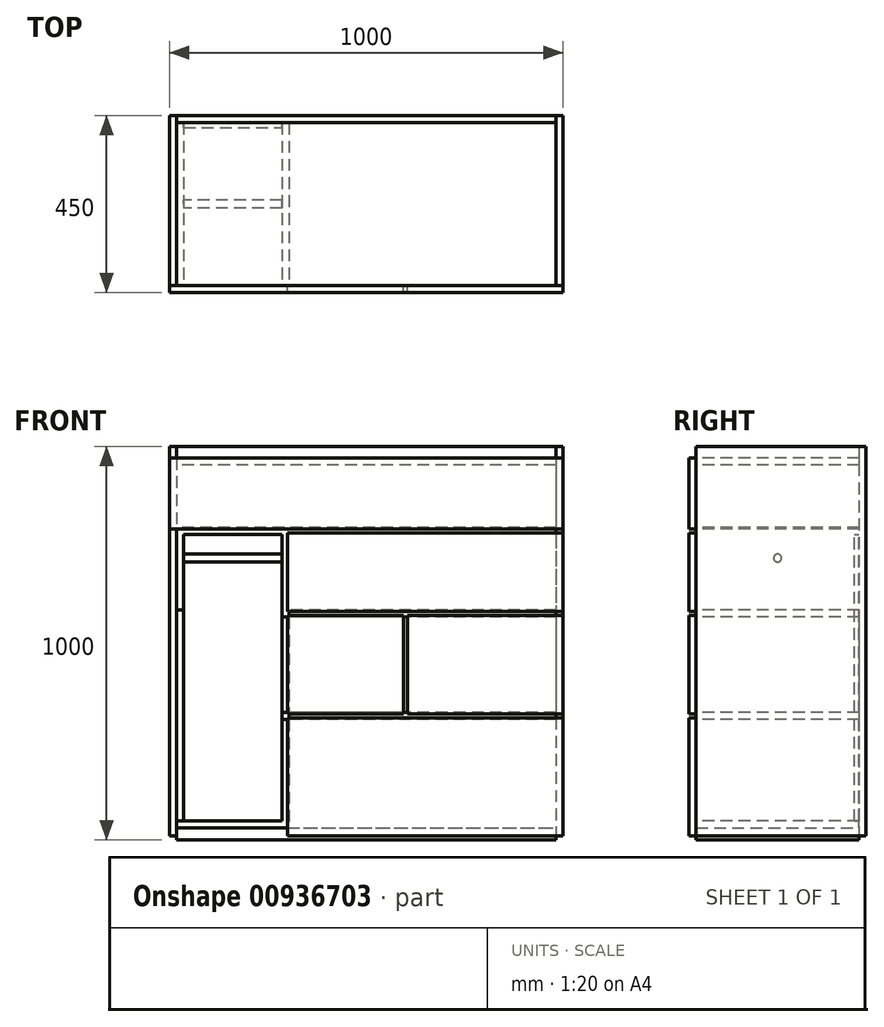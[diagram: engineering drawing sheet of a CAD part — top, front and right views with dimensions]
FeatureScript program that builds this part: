
annotation { "Feature Type Name" : "Feature", "Feature Type Description" : "" }
export const myFeature = defineFeature(function(context is Context, id is Id, definition is map)
    precondition{}
    {
        {
            var Q0;
            Q0=qCreatedBy(makeId("Top.planeOp"),FACE);
            var sketch = newSketch(context, id + "F0", { "sketchPlane" : qUnion([Q0])});
            skLineSegment(sketch, "E0.bottom", {"start": v(0, 0) * mm, "end": v(1000, 0) * mm});
            skLineSegment(sketch, "E0.top", {"start": v(0, 432) * mm, "end": v(1000, 432) * mm});
            skLineSegment(sketch, "E0.left", {"start": v(0, 0) * mm, "end": v(0, 432) * mm});
            skLineSegment(sketch, "E0.right", {"start": v(1000, 0) * mm, "end": v(1000, 432) * mm});
            skLineSegment(sketch, "E1.0", {"start": v(18, 0) * mm, "end": v(18, 432) * mm});
            skLineSegment(sketch, "E2", {"start": v(500, 467.89) * mm, "end": v(500, 549.02) * mm, "construction": true});
            skPoint(sketch, "E2.startSnap0", {"position": v(500, 432) * mm});
            skLineSegment(sketch, "E3.MirrorCS", {"start": v(982, 0) * mm, "end": v(982, 432) * mm});
            skLineSegment(sketch, "E4", {"start": v(1028.28, 216) * mm, "end": v(1100.38, 216) * mm, "construction": true});
            skPoint(sketch, "E4.startSnap0", {"position": v(1000, 216) * mm});
            skLineSegment(sketch, "E5.0", {"start": v(0, 414) * mm, "end": v(1000, 414) * mm});
            skSolve(sketch);
        }
        {
            var Q0;
            {var subQ0=sQuery(id+"F0.wireOp",EDGE,"E0.left");var subQ1=sQuery(id+"F0.wireOp",EDGE,"E0.bottom");var subQ2=makeQuery(id+"F0.imprint","INTERSECT",VERTEX,{"derivedFrom":[subQ1,subQ0]});Q0=makeQuery(id+"F0.imprint","IMPRINT",FACE,{"disambiguationData":[TD([[makeQuery(id+"F0.imprint","IMPRINT",EDGE,{"disambiguationData":[TD([[subQ2,-1.0]])],"derivedFrom":subQ1}),1.0]])]});}
            var Q1;
            {var subQ0=sQuery(id+"F0.wireOp",EDGE,"E0.left");var subQ1=sQuery(id+"F0.wireOp",EDGE,"E0.top");var subQ2=makeQuery(id+"F0.imprint","INTERSECT",VERTEX,{"derivedFrom":[subQ1,subQ0]});Q1=makeQuery(id+"F0.imprint","IMPRINT",FACE,{"disambiguationData":[TD([[makeQuery(id+"F0.imprint","IMPRINT",EDGE,{"disambiguationData":[TD([[subQ2,-1.0]])],"derivedFrom":subQ1}),-1.0]])]});}
            var Q2;
            {var subQ0=sQuery(id+"F0.wireOp",EDGE,"E0.right");var subQ1=sQuery(id+"F0.wireOp",EDGE,"E0.top");var subQ2=makeQuery(id+"F0.imprint","INTERSECT",VERTEX,{"derivedFrom":[subQ1,subQ0]});Q2=makeQuery(id+"F0.imprint","IMPRINT",FACE,{"disambiguationData":[TD([[makeQuery(id+"F0.imprint","IMPRINT",EDGE,{"disambiguationData":[TD([[subQ2,1.0]])],"derivedFrom":subQ1}),-1.0]])]});}
            var Q3;
            {var subQ0=sQuery(id+"F0.wireOp",EDGE,"E0.right");var subQ1=sQuery(id+"F0.wireOp",EDGE,"E0.bottom");var subQ2=makeQuery(id+"F0.imprint","INTERSECT",VERTEX,{"derivedFrom":[subQ1,subQ0]});Q3=makeQuery(id+"F0.imprint","IMPRINT",FACE,{"disambiguationData":[TD([[makeQuery(id+"F0.imprint","IMPRINT",EDGE,{"disambiguationData":[TD([[subQ2,1.0]])],"derivedFrom":subQ1}),1.0]])]});}
            extrude(context, id + "F1", {"entities" : qUnion([Q0, Q1, Q2, Q3]), "depth" : 990 * mm, "offsetDistance" : 25 * mm});
        }
        {
            var Q0;
            {var subQ0=sQuery(id+"F0.wireOp",EDGE,"E1.0");var subQ1=sQuery(id+"F0.wireOp",EDGE,"E0.top");var subQ2=makeQuery(id+"F0.imprint","INTERSECT",VERTEX,{"derivedFrom":[subQ1,subQ0]});Q0=makeQuery(id+"F0.imprint","IMPRINT",FACE,{"disambiguationData":[TD([[makeQuery(id+"F0.imprint","IMPRINT",EDGE,{"disambiguationData":[TD([[subQ2,-1.0]])],"derivedFrom":subQ1}),-1.0]])]});}
            var Q1;
            Q1=makeQuery(id+"F1.opExtrude","CAP_FACE",FACE,{"disambiguationData":[OSD([sQuery(id+"F0.wireOp",EDGE,"E0.bottom"),sQuery(id+"F0.wireOp",EDGE,"E0.top"),sQuery(id+"F0.wireOp",EDGE,"E0.left"),sQuery(id+"F0.wireOp",EDGE,"E1.0")])],"isStart":false});
            extrude(context, id + "F2", {"entities" : qUnion([Q0]), "endBound" : BoundingType.UP_TO_SURFACE, "depth" : 25 * mm, "endBoundEntityFace" : qUnion([Q1]), "offsetDistance" : 25 * mm});
        }
        {
            var Q0;
            {var subQ0=sQuery(id+"F0.wireOp",EDGE,"E1.0");var subQ1=sQuery(id+"F0.wireOp",EDGE,"E0.bottom");var subQ2=makeQuery(id+"F0.imprint","INTERSECT",VERTEX,{"derivedFrom":[subQ1,subQ0]});Q0=makeQuery(id+"F0.imprint","IMPRINT",FACE,{"disambiguationData":[TD([[makeQuery(id+"F0.imprint","IMPRINT",EDGE,{"disambiguationData":[TD([[subQ2,-1.0]])],"derivedFrom":subQ1}),1.0]])]});}
            extrude(context, id + "F3", {"entities" : qUnion([Q0]), "depth" : 20 * mm, "offsetDistance" : 25 * mm, "hasSecondDirection" : true, "secondDirectionOppositeDirection" : true, "secondDirectionDepth" : 10 * mm});
        }
        {
            var Q0;
            {var subQ0=sQuery(id+"F0.wireOp",EDGE,"E0.bottom");Q0=makeQuery(id+"F1.opExtrude","SWEPT_FACE",FACE,{"disambiguationData":[OSD([subQ0]),TDD([makeQuery(id+"F0.imprint","IMPRINT",EDGE,{"disambiguationData":[TD([[makeQuery(id+"F0.imprint","INTERSECT",VERTEX,{"derivedFrom":[subQ0,sQuery(id+"F0.wireOp",EDGE,"E0.left")]}),-1.0]])],"derivedFrom":subQ0})])]});}
            var sketch = newSketch(context, id + "F4", { "sketchPlane" : qUnion([Q0])});
            skLineSegment(sketch, "E6.bottom", {"start": v(1000, 560) * mm, "end": v(605, 560) * mm});
            skLineSegment(sketch, "E6.top", {"start": v(1000, 310) * mm, "end": v(605, 310) * mm});
            skLineSegment(sketch, "E6.left", {"start": v(1000, 560) * mm, "end": v(1000, 310) * mm});
            skLineSegment(sketch, "E6.right", {"start": v(605, 560) * mm, "end": v(605, 310) * mm});
            skLineSegment(sketch, "E7.bottom", {"start": v(595, 560) * mm, "end": v(0, 560) * mm});
            skLineSegment(sketch, "E7.top", {"start": v(595, 310) * mm, "end": v(0, 310) * mm});
            skLineSegment(sketch, "E7.left", {"start": v(595, 560) * mm, "end": v(595, 310) * mm});
            skLineSegment(sketch, "E7.right", {"start": v(0, 560) * mm, "end": v(0, 310) * mm});
            skLineSegment(sketch, "E8", {"start": v(605, 435) * mm, "end": v(595, 435) * mm, "construction": true});
            skLineSegment(sketch, "E9.bottom", {"start": v(0, 300) * mm, "end": v(290, 300) * mm});
            skLineSegment(sketch, "E9.top", {"start": v(0, 0) * mm, "end": v(290, 0) * mm});
            skLineSegment(sketch, "E9.right", {"start": v(290, 300) * mm, "end": v(290, 0) * mm});
            skLineSegment(sketch, "E10.bottom", {"start": v(300, 300) * mm, "end": v(1000, 300) * mm});
            skLineSegment(sketch, "E10.top", {"start": v(300, 0) * mm, "end": v(1000, 0) * mm});
            skLineSegment(sketch, "E10.left", {"start": v(300, 300) * mm, "end": v(300, 0) * mm});
            skLineSegment(sketch, "E10.right", {"start": v(1000, 300) * mm, "end": v(1000, 0) * mm});
            skLineSegment(sketch, "E11", {"start": v(10.26, 310) * mm, "end": v(10.26, 300) * mm, "construction": true});
            skLineSegment(sketch, "E12", {"start": v(300, 150) * mm, "end": v(290, 150) * mm, "construction": true});
            skLineSegment(sketch, "E13.bottom", {"start": v(1000, 770) * mm, "end": v(300, 770) * mm});
            skLineSegment(sketch, "E13.top", {"start": v(1000, 570) * mm, "end": v(300, 570) * mm});
            skLineSegment(sketch, "E13.left", {"start": v(1000, 770) * mm, "end": v(1000, 570) * mm});
            skLineSegment(sketch, "E13.right", {"start": v(300, 770) * mm, "end": v(300, 570) * mm});
            skLineSegment(sketch, "E14.bottom", {"start": v(290, 770) * mm, "end": v(0, 770) * mm});
            skLineSegment(sketch, "E14.top", {"start": v(290, 570) * mm, "end": v(0, 570) * mm});
            skLineSegment(sketch, "E14.left", {"start": v(290, 770) * mm, "end": v(290, 570) * mm});
            skLineSegment(sketch, "E14.right", {"start": v(0, 770) * mm, "end": v(0, 570) * mm});
            skLineSegment(sketch, "E15", {"start": v(277.64, 570) * mm, "end": v(277.64, 560) * mm, "construction": true});
            skLineSegment(sketch, "E16", {"start": v(300, 629.54) * mm, "end": v(290, 629.54) * mm, "construction": true});
            skLineSegment(sketch, "E17.bottom", {"start": v(0, 990) * mm, "end": v(1000, 990) * mm});
            skLineSegment(sketch, "E17.top", {"start": v(0, 780) * mm, "end": v(1000, 780) * mm});
            skLineSegment(sketch, "E17.left", {"start": v(0, 990) * mm, "end": v(0, 780) * mm});
            skLineSegment(sketch, "E17.right", {"start": v(1000, 990) * mm, "end": v(1000, 780) * mm});
            skLineSegment(sketch, "E18", {"start": v(-67.03, 780) * mm, "end": v(-67.03, 770) * mm, "construction": true});
            skLineSegment(sketch, "E19", {"start": v(0, 300) * mm, "end": v(0, 0) * mm});
            skLineSegment(sketch, "E20", {"start": v(0, 960) * mm, "end": v(1000, 960) * mm});
            skLineSegment(sketch, "E21", {"start": v(300, 560) * mm, "end": v(300, 310) * mm});
            skSolve(sketch);
        }
        {
            var Q0;
            {var subQ0=sQuery(id+"F4.wireOp",EDGE,"E17.right");var subQ1=sQuery(id+"F4.wireOp",EDGE,"E17.top");var subQ2=makeQuery(id+"F4.imprint","INTERSECT",VERTEX,{"derivedFrom":[subQ1,subQ0]});Q0=makeQuery(id+"F4.imprint","IMPRINT",FACE,{"disambiguationData":[TD([[makeQuery(id+"F4.imprint","IMPRINT",EDGE,{"disambiguationData":[TD([[subQ2,1.0]])],"derivedFrom":subQ0}),-1.0]])]});}
            var Q1;
            {var subQ0=sQuery(id+"F4.wireOp",EDGE,"E17.left");var subQ6=sQuery(id+"F4.wireOp",EDGE,"E20");var subQ7=makeQuery(id+"F4.imprint","INTERSECT",VERTEX,{"derivedFrom":[subQ0,subQ6]});Q1=makeQuery(id+"F4.imprint","IMPRINT",FACE,{"disambiguationData":[TD([[makeQuery(id+"F4.imprint","IMPRINT",EDGE,{"disambiguationData":[TD([[subQ7,-1.0]])],"derivedFrom":subQ6}),-1.0]])]});}
            var Q2;
            Q2=makeQuery(id+"F4.imprint","IMPRINT",FACE,{"disambiguationData":[TD([[makeQuery(id+"F4.imprint","IMPRINT",EDGE,{"derivedFrom":sQuery(id+"F4.wireOp",EDGE,"E13.bottom")}),1.0]])]});
            var Q3;
            Q3=makeQuery(id+"F4.imprint","IMPRINT",FACE,{"disambiguationData":[TD([[makeQuery(id+"F4.imprint","IMPRINT",EDGE,{"derivedFrom":sQuery(id+"F4.wireOp",EDGE,"E6.bottom")}),1.0]])]});
            var Q4;
            Q4=makeQuery(id+"F4.imprint","IMPRINT",FACE,{"disambiguationData":[TD([[makeQuery(id+"F4.imprint","IMPRINT",EDGE,{"derivedFrom":sQuery(id+"F4.wireOp",EDGE,"E10.bottom")}),-1.0]])]});
            var Q5;
            {var subQ0=sQuery(id+"F4.wireOp",EDGE,"E7.left");Q5=makeQuery(id+"F4.imprint","IMPRINT",FACE,{"disambiguationData":[TD([[makeQuery(id+"F4.imprint","IMPRINT",EDGE,{"derivedFrom":subQ0}),-1.0]])]});}
            extrude(context, id + "F5", {"entities" : qUnion([Q0, Q1, Q2, Q3, Q4, Q5]), "depth" : 18 * mm, "offsetDistance" : 25 * mm});
        }
        {
            var Q0;
            Q0=makeQuery(id+"F5.opExtrude","CAP_FACE",FACE,{"disambiguationData":[OSD([sQuery(id+"F4.wireOp",EDGE,"E17.top"),sQuery(id+"F4.wireOp",EDGE,"E17.left"),sQuery(id+"F4.wireOp",EDGE,"E17.right"),sQuery(id+"F4.wireOp",EDGE,"E20")])],"isStart":true});
            var sketch = newSketch(context, id + "F6", { "sketchPlane" : qUnion([Q0])});
            skLineSegment(sketch, "E22.bottom", {"start": v(-982, 784) * mm, "end": v(-18, 784) * mm});
            skLineSegment(sketch, "E22.top", {"start": v(-982, 766) * mm, "end": v(-18, 766) * mm});
            skLineSegment(sketch, "E22.left", {"start": v(-982, 784) * mm, "end": v(-982, 766) * mm});
            skLineSegment(sketch, "E22.right", {"start": v(-18, 784) * mm, "end": v(-18, 766) * mm});
            skLineSegment(sketch, "E23", {"start": v(-903.66, 780) * mm, "end": v(-903.66, 770) * mm, "construction": true});
            skLineSegment(sketch, "E24", {"start": v(-878.2, 570) * mm, "end": v(-878.2, 560) * mm, "construction": true});
            skLineSegment(sketch, "E25", {"start": v(-871.46, 310) * mm, "end": v(-871.46, 300) * mm, "construction": true});
            skLineSegment(sketch, "E26", {"start": v(-605, 441.3) * mm, "end": v(-605, 441.3) * mm});
            skLineSegment(sketch, "E27", {"start": v(-300, 157.99) * mm, "end": v(-290, 157.99) * mm, "construction": true});
            skPoint(sketch, "E28", {"position": v(-903.66, 775) * mm});
            skPoint(sketch, "E29", {"position": v(-878.2, 565) * mm});
            skPoint(sketch, "E30", {"position": v(-605, 441.3) * mm});
            skPoint(sketch, "E31", {"position": v(-871.46, 305) * mm});
            skPoint(sketch, "E32", {"position": v(-295, 157.99) * mm});
            skPoint(sketch, "E33", {"position": v(-982, 775) * mm});
            skLineSegment(sketch, "E34.bottom", {"start": v(-982, 574) * mm, "end": v(-18, 574) * mm});
            skLineSegment(sketch, "E34.top", {"start": v(-982, 556) * mm, "end": v(-18, 556) * mm});
            skLineSegment(sketch, "E34.left", {"start": v(-982, 574) * mm, "end": v(-982, 556) * mm});
            skLineSegment(sketch, "E34.right", {"start": v(-18, 574) * mm, "end": v(-18, 556) * mm});
            skLineSegment(sketch, "E35.bottom", {"start": v(-982, 314) * mm, "end": v(-18, 314) * mm});
            skLineSegment(sketch, "E35.top", {"start": v(-982, 296) * mm, "end": v(-18, 296) * mm});
            skLineSegment(sketch, "E35.left", {"start": v(-982, 314) * mm, "end": v(-982, 296) * mm});
            skLineSegment(sketch, "E35.right", {"start": v(-18, 314) * mm, "end": v(-18, 296) * mm});
            skLineSegment(sketch, "E36.bottom", {"start": v(-304, 296) * mm, "end": v(-286, 296) * mm});
            skLineSegment(sketch, "E36.top", {"start": v(-304, 20) * mm, "end": v(-286, 20) * mm});
            skLineSegment(sketch, "E36.left", {"start": v(-304, 296) * mm, "end": v(-304, 20) * mm});
            skLineSegment(sketch, "E36.right", {"start": v(-286, 296) * mm, "end": v(-286, 20) * mm});
            skLineSegment(sketch, "E37.bottom", {"start": v(-614, 556) * mm, "end": v(-596, 556) * mm});
            skLineSegment(sketch, "E37.top", {"start": v(-614, 314) * mm, "end": v(-596, 314) * mm});
            skLineSegment(sketch, "E37.left", {"start": v(-614, 556) * mm, "end": v(-614, 314) * mm});
            skLineSegment(sketch, "E37.right", {"start": v(-596, 556) * mm, "end": v(-596, 314) * mm});
            skLineSegment(sketch, "E38.bottom", {"start": v(-304, 766) * mm, "end": v(-286, 766) * mm});
            skLineSegment(sketch, "E38.top", {"start": v(-304, 574) * mm, "end": v(-286, 574) * mm});
            skLineSegment(sketch, "E38.left", {"start": v(-304, 766) * mm, "end": v(-304, 574) * mm});
            skLineSegment(sketch, "E38.right", {"start": v(-286, 766) * mm, "end": v(-286, 574) * mm});
            skLineSegment(sketch, "E39.bottom", {"start": v(-36, 766) * mm, "end": v(-18, 766) * mm});
            skLineSegment(sketch, "E39.top", {"start": v(-36, 574) * mm, "end": v(-18, 574) * mm});
            skLineSegment(sketch, "E39.left", {"start": v(-36, 766) * mm, "end": v(-36, 574) * mm});
            skLineSegment(sketch, "E39.right", {"start": v(-18, 766) * mm, "end": v(-18, 574) * mm});
            skPoint(sketch, "E40", {"position": v(-982, 565) * mm});
            skPoint(sketch, "E41", {"position": v(-605, 556) * mm});
            skPoint(sketch, "E42", {"position": v(-982, 305) * mm});
            skPoint(sketch, "E43", {"position": v(-295, 296) * mm});
            skLineSegment(sketch, "E44.bottom", {"start": v(-982, 960) * mm, "end": v(-18, 960) * mm});
            skLineSegment(sketch, "E44.top", {"start": v(-982, 942) * mm, "end": v(-18, 942) * mm});
            skLineSegment(sketch, "E44.left", {"start": v(-982, 960) * mm, "end": v(-982, 942) * mm});
            skLineSegment(sketch, "E44.right", {"start": v(-18, 960) * mm, "end": v(-18, 942) * mm});
            skLineSegment(sketch, "E45", {"start": v(-304, 574) * mm, "end": v(-304, 296) * mm});
            skLineSegment(sketch, "E46", {"start": v(-286, 574) * mm, "end": v(-286, 296) * mm});
            skLineSegment(sketch, "E47", {"start": v(-36, 574) * mm, "end": v(-36, 20) * mm});
            skLineSegment(sketch, "E48", {"start": v(-36, 20) * mm, "end": v(-18, 20) * mm});
            skLineSegment(sketch, "E49", {"start": v(-18, 20) * mm, "end": v(-18, 556) * mm});
            skLineSegment(sketch, "E50", {"start": v(-304, 38) * mm, "end": v(-18, 38) * mm});
            skLineSegment(sketch, "E51", {"start": v(-304, 20) * mm, "end": v(-18, 20) * mm});
            skSolve(sketch);
        }
        {
            var Q0;
            Q0=makeQuery(id+"F6.imprint","IMPRINT",FACE,{"disambiguationData":[TD([[makeQuery(id+"F6.imprint","IMPRINT",EDGE,{"derivedFrom":sQuery(id+"F6.wireOp",EDGE,"E44.bottom")}),1.0]])]});
            var Q1;
            {var subQ6=sQuery(id+"F6.wireOp",EDGE,"E38.bottom");Q1=makeQuery(id+"F6.imprint","IMPRINT",FACE,{"disambiguationData":[TD([[makeQuery(id+"F6.imprint","IMPRINT",EDGE,{"derivedFrom":subQ6}),1.0]])]});}
            var Q2;
            {var subQ0=sQuery(id+"F6.wireOp",EDGE,"E22.bottom");Q2=makeQuery(id+"F6.imprint","IMPRINT",FACE,{"disambiguationData":[TD([[makeQuery(id+"F6.imprint","IMPRINT",EDGE,{"derivedFrom":subQ0}),-1.0]])]});}
            var Q3;
            {var subQ4=sQuery(id+"F6.wireOp",EDGE,"E34.left");Q3=makeQuery(id+"F6.imprint","IMPRINT",FACE,{"disambiguationData":[TD([[makeQuery(id+"F6.imprint","IMPRINT",EDGE,{"derivedFrom":subQ4}),1.0]])]});}
            var Q4;
            {var subQ3=sQuery(id+"F6.wireOp",EDGE,"E35.left");Q4=makeQuery(id+"F6.imprint","IMPRINT",FACE,{"disambiguationData":[TD([[makeQuery(id+"F6.imprint","IMPRINT",EDGE,{"derivedFrom":subQ3}),1.0]])]});}
            var Q5;
            Q5=makeQuery(id+"F6.imprint","IMPRINT",FACE,{"disambiguationData":[TD([[makeQuery(id+"F6.imprint","IMPRINT",EDGE,{"derivedFrom":sQuery(id+"F6.wireOp",EDGE,"QM6Bufxx-I5ZU-JCkN-k9jX-k9IJHGgFzfra.bottom")}),1.0]])]});
            var Q6;
            {var subQ0=sQuery(id+"F6.wireOp",EDGE,"E51");var subQ1=sQuery(id+"F6.wireOp",EDGE,"E36.left");var subQ2=makeQuery(id+"F6.imprint","INTERSECT",VERTEX,{"derivedFrom":[subQ1,subQ0]});Q6=makeQuery(id+"F6.imprint","IMPRINT",FACE,{"disambiguationData":[TD([[makeQuery(id+"F6.imprint","IMPRINT",EDGE,{"disambiguationData":[TD([[subQ2,1.0]])],"derivedFrom":subQ1}),1.0]])]});}
            var Q7;
            {var subQ0=sQuery(id+"F6.wireOp",EDGE,"E51");var subQ1=sQuery(id+"F6.wireOp",EDGE,"E36.right");var subQ2=makeQuery(id+"F6.imprint","INTERSECT",VERTEX,{"derivedFrom":[subQ1,subQ0]});Q7=makeQuery(id+"F6.imprint","IMPRINT",FACE,{"disambiguationData":[TD([[makeQuery(id+"F6.imprint","IMPRINT",EDGE,{"disambiguationData":[TD([[subQ2,1.0]])],"derivedFrom":subQ1}),1.0]])]});}
            var Q8;
            {var subQ0=sQuery(id+"F6.wireOp",EDGE,"E51");var subQ1=sQuery(id+"F6.wireOp",EDGE,"E47");var subQ2=makeQuery(id+"F6.imprint","INTERSECT",VERTEX,{"derivedFrom":[subQ1,subQ0]});Q8=makeQuery(id+"F6.imprint","IMPRINT",FACE,{"disambiguationData":[TD([[makeQuery(id+"F6.imprint","IMPRINT",EDGE,{"disambiguationData":[TD([[subQ2,1.0]])],"derivedFrom":subQ1}),1.0]])]});}
            var Q9;
            Q9=makeQuery(id+"F2.opExtrude","SWEPT_FACE",FACE,{"disambiguationData":[OSD([sQuery(id+"F0.wireOp",EDGE,"E5.0")])]});
            extrude(context, id + "F7", {"entities" : qUnion([Q0, Q1, Q2, Q3, Q4, Q5, Q6, Q7, Q8]), "endBound" : BoundingType.UP_TO_SURFACE, "depth" : 25 * mm, "endBoundEntityFace" : qUnion([Q9]), "offsetDistance" : 25 * mm});
        }
        {
            var Q0;
            Q0=makeQuery(id+"F6.imprint","IMPRINT",FACE,{"disambiguationData":[TD([[makeQuery(id+"F6.imprint","IMPRINT",EDGE,{"derivedFrom":sQuery(id+"F6.wireOp",EDGE,"E38.bottom")}),-1.0]])]});
            var Q1;
            Q1=makeQuery(id+"F6.imprint","IMPRINT",FACE,{"disambiguationData":[TD([[makeQuery(id+"F6.imprint","IMPRINT",EDGE,{"derivedFrom":sQuery(id+"F6.wireOp",EDGE,"E37.bottom")}),-1.0]])]});
            var Q2;
            Q2=makeQuery(id+"F6.imprint","IMPRINT",FACE,{"disambiguationData":[TD([[makeQuery(id+"F6.imprint","IMPRINT",EDGE,{"derivedFrom":sQuery(id+"F6.wireOp",EDGE,"E36.bottom")}),-1.0]])]});
            var Q3;
            Q3=makeQuery(id+"F6.imprint","IMPRINT",FACE,{"disambiguationData":[TD([[makeQuery(id+"F6.imprint","IMPRINT",EDGE,{"derivedFrom":sQuery(id+"F6.wireOp",EDGE,"E39.bottom")}),-1.0]])]});
            var Q4;
            {var subQ5=sQuery(id+"F6.wireOp",EDGE,"E36.bottom");Q4=makeQuery(id+"F6.imprint","IMPRINT",FACE,{"disambiguationData":[TD([[makeQuery(id+"F6.imprint","IMPRINT",EDGE,{"derivedFrom":subQ5}),1.0]])]});}
            var Q5;
            {var subQ0=sQuery(id+"F6.wireOp",EDGE,"E45");var subQ1=sQuery(id+"F6.wireOp",EDGE,"E34.top");var subQ2=makeQuery(id+"F6.imprint","INTERSECT",VERTEX,{"derivedFrom":[subQ1,subQ0]});Q5=makeQuery(id+"F6.imprint","IMPRINT",FACE,{"disambiguationData":[TD([[makeQuery(id+"F6.imprint","IMPRINT",EDGE,{"disambiguationData":[TD([[subQ2,-1.0]])],"derivedFrom":subQ1}),-1.0]])]});}
            var Q6;
            {var subQ5=sQuery(id+"F6.wireOp",EDGE,"E38.top");Q6=makeQuery(id+"F6.imprint","IMPRINT",FACE,{"disambiguationData":[TD([[makeQuery(id+"F6.imprint","IMPRINT",EDGE,{"derivedFrom":subQ5}),-1.0]])]});}
            var Q7;
            {var subQ0=sQuery(id+"F6.wireOp",EDGE,"E34.right");Q7=makeQuery(id+"F6.imprint","IMPRINT",FACE,{"disambiguationData":[TD([[makeQuery(id+"F6.imprint","IMPRINT",EDGE,{"derivedFrom":subQ0}),-1.0]])]});}
            var Q8;
            {var subQ0=sQuery(id+"F6.wireOp",EDGE,"E49");var subQ5=sQuery(id+"F6.wireOp",EDGE,"E35.bottom");var subQ7=makeQuery(id+"F6.imprint","INTERSECT",VERTEX,{"derivedFrom":[subQ5,subQ0]});Q8=makeQuery(id+"F6.imprint","IMPRINT",FACE,{"disambiguationData":[TD([[makeQuery(id+"F6.imprint","IMPRINT",EDGE,{"disambiguationData":[TD([[subQ7,1.0]])],"derivedFrom":subQ5}),1.0]])]});}
            var Q9;
            {var subQ0=sQuery(id+"F6.wireOp",EDGE,"E49");var subQ1=sQuery(id+"F6.wireOp",EDGE,"E35.bottom");var subQ2=makeQuery(id+"F6.imprint","INTERSECT",VERTEX,{"derivedFrom":[subQ1,subQ0]});Q9=makeQuery(id+"F6.imprint","IMPRINT",FACE,{"disambiguationData":[TD([[makeQuery(id+"F6.imprint","IMPRINT",EDGE,{"disambiguationData":[TD([[subQ2,1.0]])],"derivedFrom":subQ1}),-1.0]])]});}
            var Q10;
            {var subQ0=sQuery(id+"F6.wireOp",EDGE,"E49");var subQ1=sQuery(id+"F6.wireOp",EDGE,"E35.top");var subQ2=makeQuery(id+"F6.imprint","INTERSECT",VERTEX,{"derivedFrom":[subQ1,subQ0]});Q10=makeQuery(id+"F6.imprint","IMPRINT",FACE,{"disambiguationData":[TD([[makeQuery(id+"F6.imprint","IMPRINT",EDGE,{"disambiguationData":[TD([[subQ2,1.0]])],"derivedFrom":subQ1}),-1.0]])]});}
            var Q11;
            Q11=makeQuery(id+"F7.opExtrude","CAP_FACE",FACE,{"disambiguationData":[OSD([sQuery(id+"F6.wireOp",EDGE,"E34.bottom"),sQuery(id+"F6.wireOp",EDGE,"E34.top"),sQuery(id+"F6.wireOp",EDGE,"E34.left"),sQuery(id+"F6.wireOp",EDGE,"E34.right"),sQuery(id+"F6.wireOp",EDGE,"E37.bottom"),sQuery(id+"F6.wireOp",EDGE,"E38.top"),sQuery(id+"F6.wireOp",EDGE,"E39.top")])],"isStart":false});
            extrude(context, id + "F8", {"entities" : qUnion([Q0, Q1, Q2, Q3, Q4, Q5, Q6, Q7, Q8, Q9, Q10]), "endBound" : BoundingType.UP_TO_SURFACE, "depth" : 25 * mm, "endBoundEntityFace" : qUnion([Q11]), "offsetDistance" : 25 * mm});
        }
        {
            var Q0;
            Q0=makeQuery(id+"F8.opExtrude","SWEPT_FACE",FACE,{"disambiguationData":[OSD([sQuery(id+"F6.wireOp",EDGE,"E39.left"),sQuery(id+"F6.wireOp",EDGE,"E47")])]});
            var sketch = newSketch(context, id + "F9", { "sketchPlane" : qUnion([Q0])});
            skLineSegment(sketch, "E52", {"start": v(207, 766) * mm, "end": v(207, 706) * mm, "construction": true});
            skCircle(sketch, "E53", {"center": v(207, 706) * mm, "radius": 10 * mm});
            skPoint(sketch, "E54", {"position": v(207, 766) * mm});
            skSolve(sketch);
        }
        {
            var Q0;
            Q0=makeQuery(id+"F9.imprint","IMPRINT",FACE,{"disambiguationData":[TD([[makeQuery(id+"F9.imprint","IMPRINT",EDGE,{"derivedFrom":sQuery(id+"F9.wireOp",EDGE,"E53")}),1.0]])]});
            var Q1;
            Q1=sQuery(id+"F9.wireOp",EDGE,"E53");
            var Q2;
            Q2=makeQuery(id+"F8.opExtrude","SWEPT_FACE",FACE,{"disambiguationData":[OSD([sQuery(id+"F6.wireOp",EDGE,"E36.right"),sQuery(id+"F6.wireOp",EDGE,"E38.right"),sQuery(id+"F6.wireOp",EDGE,"E46")])]});
            extrude(context, id + "F10", {"entities" : qUnion([Q0]), "surfaceEntities" : qUnion([Q1]), "endBound" : BoundingType.UP_TO_SURFACE, "depth" : 25 * mm, "endBoundEntityFace" : qUnion([Q2]), "offsetDistance" : 25 * mm});
        }
        {
            var Q0;
            Q0=makeQuery(id+"F2.opExtrude","SWEPT_FACE",FACE,{"disambiguationData":[OSD([sQuery(id+"F0.wireOp",EDGE,"E5.0")])]});
            var sketch = newSketch(context, id + "F11", { "sketchPlane" : qUnion([Q0])});
            skLineSegment(sketch, "E55.bottom", {"start": v(36, 38) * mm, "end": v(286, 38) * mm});
            skLineSegment(sketch, "E55.top", {"start": v(36, 766) * mm, "end": v(286, 766) * mm});
            skLineSegment(sketch, "E55.left", {"start": v(36, 38) * mm, "end": v(36, 766) * mm});
            skLineSegment(sketch, "E55.right", {"start": v(286, 38) * mm, "end": v(286, 766) * mm});
            skSolve(sketch);
        }
        {
            var Q0;
            Q0=makeQuery(id+"F11.imprint","IMPRINT",FACE,{"disambiguationData":[TD([[makeQuery(id+"F11.imprint","IMPRINT",EDGE,{"derivedFrom":sQuery(id+"F11.wireOp",EDGE,"E55.bottom")}),1.0]])]});
            extrude(context, id + "F12", {"entities" : qUnion([Q0]), "depth" : 12 * mm, "offsetDistance" : 25 * mm});
        }
    });
